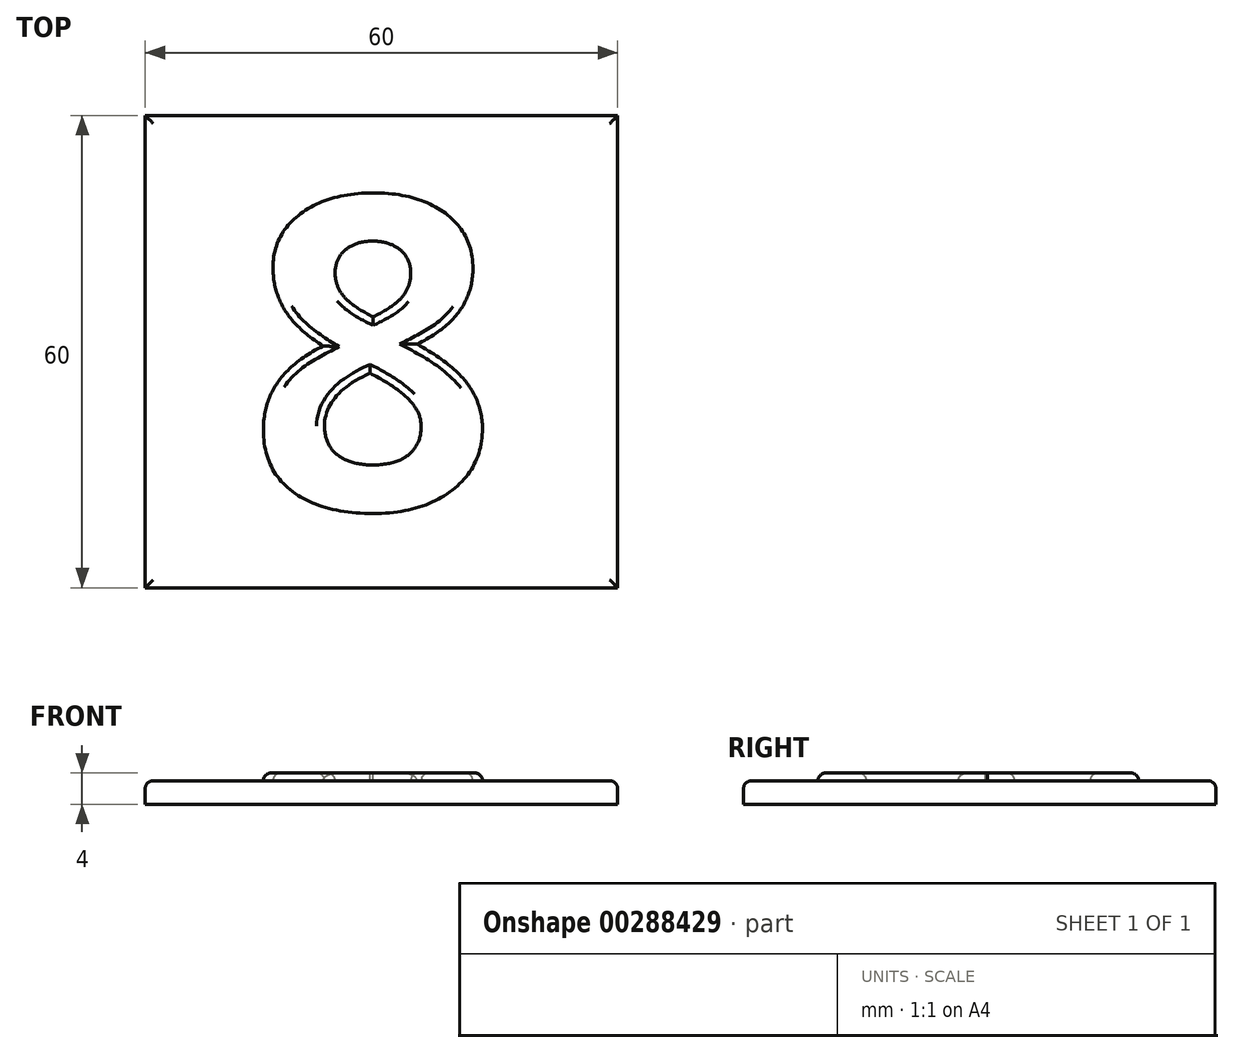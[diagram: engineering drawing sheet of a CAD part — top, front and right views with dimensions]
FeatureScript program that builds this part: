
annotation { "Feature Type Name" : "Feature", "Feature Type Description" : "" }
export const myFeature = defineFeature(function(context is Context, id is Id, definition is map)
    precondition{}
    {
        {
            var Q0;
            Q0=qCreatedBy(makeId("Top.planeOp"),FACE);
            var sketch = newSketch(context, id + "F0", { "sketchPlane" : qUnion([Q0])});
            skLineSegment(sketch, "E0.bottom", {"start": v(30, 30) * mm, "end": v(-30, 30) * mm});
            skLineSegment(sketch, "E0.top", {"start": v(30, -30) * mm, "end": v(-30, -30) * mm});
            skLineSegment(sketch, "E0.left", {"start": v(30, 30) * mm, "end": v(30, -30) * mm});
            skLineSegment(sketch, "E0.right", {"start": v(-30, 30) * mm, "end": v(-30, -30) * mm});
            skPoint(sketch, "E0.middle", {"position": v(0, 0) * mm});
            skSolve(sketch);
        }
        {
            var Q0;
            Q0 = qSketchRegion(id + "F0", true);
            extrude(context, id + "F1", {"entities" : qUnion([Q0]), "depth" : 3 * mm});
        }
        {
            var Q0;
            Q0=qCreatedBy(makeId("Top.planeOp"),FACE);
            var sketch = newSketch(context, id + "F2", { "sketchPlane" : qUnion([Q0])});
            skText(sketch, "E1", { "text": "8", "fontName": "OpenSans-Bold.ttf"});
            const initialGuessF2  = {"E1": [-0.01695, -0.02, 1, 0, 0.04]};
            skSetInitialGuess(sketch, initialGuessF2);
            skSolve(sketch);
        }
        {
            var Q0;
            Q0 = qSketchRegion(id + "F2", true);
            extrude(context, id + "F3", {"entities" : qUnion([Q0]), "operationType" : NewBodyOperationType.ADD, "depth" : 4 * mm});
        }
        {
            var Q0;
            Q0=makeQuery(id+"F1.opExtrude","CAP_EDGE",EDGE,{"disambiguationData":[OSD([sQuery(id+"F0.wireOp",EDGE,"E0.left")])],"isStart":false});
            var Q1;
            Q1=makeQuery(id+"F1.opExtrude","CAP_EDGE",EDGE,{"disambiguationData":[OSD([sQuery(id+"F0.wireOp",EDGE,"E0.bottom")])],"isStart":false});
            var Q2;
            Q2=makeQuery(id+"F1.opExtrude","CAP_EDGE",EDGE,{"disambiguationData":[OSD([sQuery(id+"F0.wireOp",EDGE,"E0.right")])],"isStart":false});
            var Q3;
            Q3=makeQuery(id+"F1.opExtrude","CAP_EDGE",EDGE,{"disambiguationData":[OSD([sQuery(id+"F0.wireOp",EDGE,"E0.top")])],"isStart":false});
            fillet(context, id + "F4", {"entities" : qUnion([Q0, Q1, Q2, Q3]), "radius" : 1 * mm, "tangentPropagation" : true, "allowEdgeOverflow" : false});
        }
        {
            var Q0;
            Q0=makeQuery(id+"F3.opExtrude","CAP_FACE",FACE,{"disambiguationData":[OSD([sQuery(id+"F2.wireOp",EDGE,"E1.sketch_text.stroke-0"),sQuery(id+"F2.wireOp",EDGE,"E1.sketch_text.stroke-1"),sQuery(id+"F2.wireOp",EDGE,"E1.sketch_text.stroke-2"),sQuery(id+"F2.wireOp",EDGE,"E1.sketch_text.stroke-3"),sQuery(id+"F2.wireOp",EDGE,"E1.sketch_text.stroke-4"),sQuery(id+"F2.wireOp",EDGE,"E1.sketch_text.stroke-5"),sQuery(id+"F2.wireOp",EDGE,"E1.sketch_text.stroke-6"),sQuery(id+"F2.wireOp",EDGE,"E1.sketch_text.stroke-7"),sQuery(id+"F2.wireOp",EDGE,"E1.sketch_text.stroke-8"),sQuery(id+"F2.wireOp",EDGE,"E1.sketch_text.stroke-9"),sQuery(id+"F2.wireOp",EDGE,"E1.sketch_text.stroke-10"),sQuery(id+"F2.wireOp",EDGE,"E1.sketch_text.stroke-11"),sQuery(id+"F2.wireOp",EDGE,"E1.sketch_text.stroke-12"),sQuery(id+"F2.wireOp",EDGE,"E1.sketch_text.stroke-13"),sQuery(id+"F2.wireOp",EDGE,"E1.sketch_text.stroke-14"),sQuery(id+"F2.wireOp",EDGE,"E1.sketch_text.stroke-15"),sQuery(id+"F2.wireOp",EDGE,"E1.sketch_text.stroke-16"),sQuery(id+"F2.wireOp",EDGE,"E1.sketch_text.stroke-17"),sQuery(id+"F2.wireOp",EDGE,"E1.sketch_text.stroke-18"),sQuery(id+"F2.wireOp",EDGE,"E1.sketch_text.stroke-19"),sQuery(id+"F2.wireOp",EDGE,"E1.sketch_text.stroke-20"),sQuery(id+"F2.wireOp",EDGE,"E1.sketch_text.stroke-21"),sQuery(id+"F2.wireOp",EDGE,"E1.sketch_text.stroke-22"),sQuery(id+"F2.wireOp",EDGE,"E1.sketch_text.stroke-23"),sQuery(id+"F2.wireOp",EDGE,"E1.sketch_text.stroke-24"),sQuery(id+"F2.wireOp",EDGE,"E1.sketch_text.stroke-25"),sQuery(id+"F2.wireOp",EDGE,"E1.sketch_text.stroke-26"),sQuery(id+"F2.wireOp",EDGE,"E1.sketch_text.stroke-27"),sQuery(id+"F2.wireOp",EDGE,"E1.sketch_text.stroke-28"),sQuery(id+"F2.wireOp",EDGE,"E1.sketch_text.stroke-29"),sQuery(id+"F2.wireOp",EDGE,"E1.sketch_text.stroke-30")])],"isStart":false});
            fillet(context, id + "F5", {"entities" : qUnion([Q0]), "radius" : 1 * mm, "tangentPropagation" : true, "allowEdgeOverflow" : false});
        }
    });
